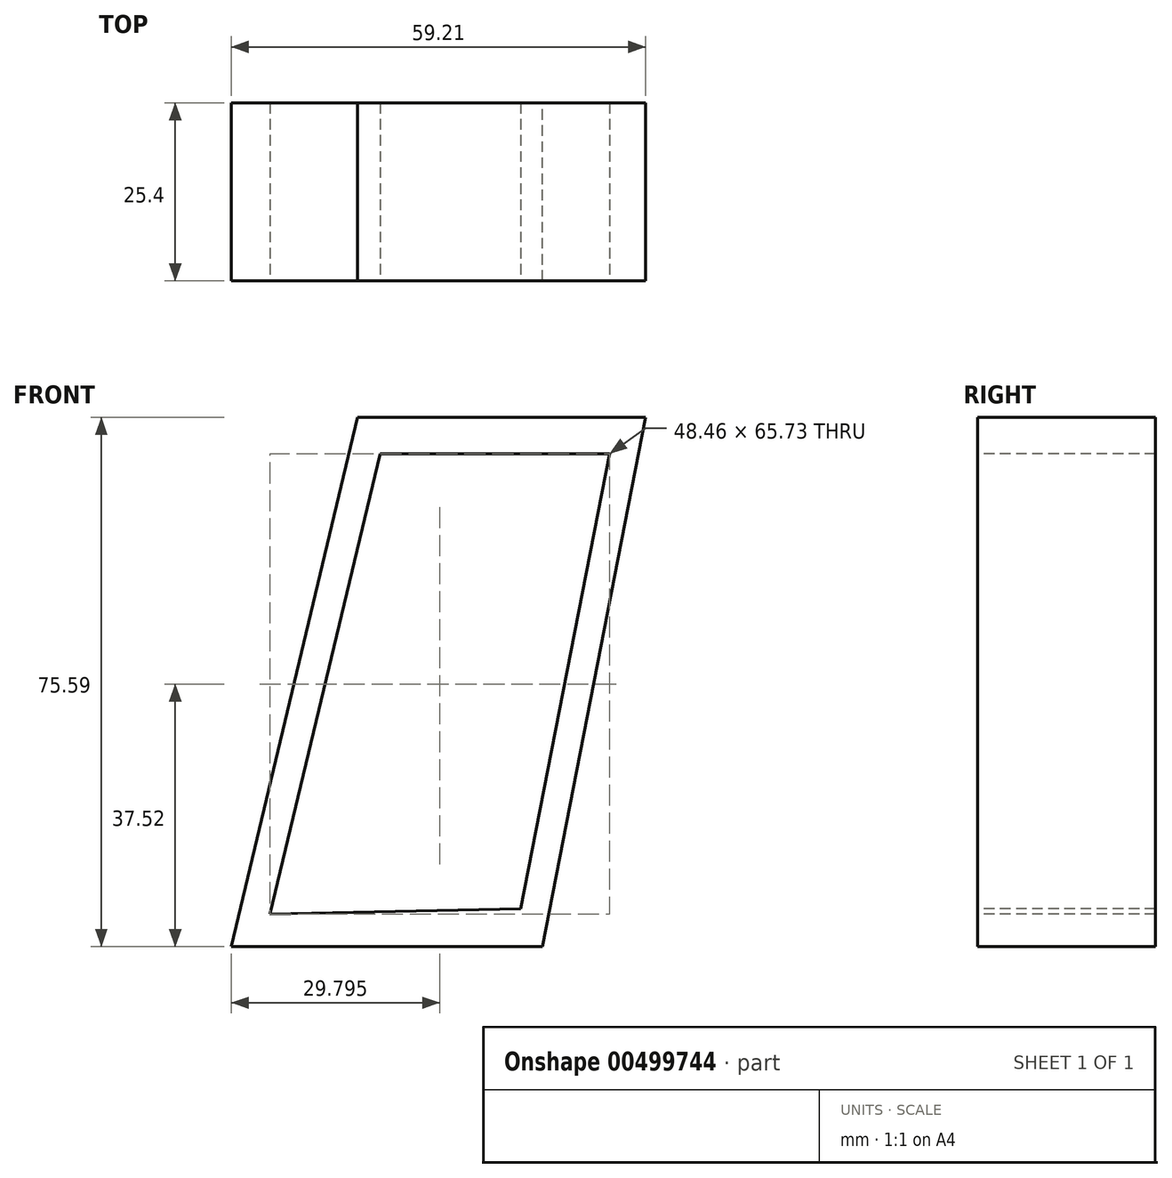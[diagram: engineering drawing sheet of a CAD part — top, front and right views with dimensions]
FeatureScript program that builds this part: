
annotation { "Feature Type Name" : "Feature", "Feature Type Description" : "" }
export const myFeature = defineFeature(function(context is Context, id is Id, definition is map)
    precondition{}
    {
        {
            var Q0;
            Q0=qCreatedBy(makeId("Front.planeOp"),FACE);
            var sketch = newSketch(context, id + "F0", { "sketchPlane" : qUnion([Q0])});
            skLineSegment(sketch, "E0", {"start": v(-26.4, 53.23) * mm, "end": v(14.76, 53.23) * mm});
            skLineSegment(sketch, "E1", {"start": v(-26.4, 53.23) * mm, "end": v(-26.4, -22.36) * mm});
            skLineSegment(sketch, "E2", {"start": v(14.76, 53.23) * mm, "end": v(-44.45, -22.36) * mm});
            skLineSegment(sketch, "E3", {"start": v(14.76, 53.23) * mm, "end": v(0, -22.36) * mm});
            skLineSegment(sketch, "E4", {"start": v(0, -22.36) * mm, "end": v(-44.45, -22.36) * mm});
            skLineSegment(sketch, "E5", {"start": v(0, -22.36) * mm, "end": v(-26.4, 53.23) * mm});
            skLineSegment(sketch, "E6", {"start": v(-44.45, -22.36) * mm, "end": v(-26.4, 53.23) * mm});
            skSolve(sketch);
        }
        {
            var Q0;
            Q0 = qSketchRegion(id + "F0", true);
            extrude(context, id + "F1", {"entities" : qUnion([Q0]), "depth" : 25.4 * mm});
        }
        {
            var Q0;
            Q0=makeQuery(id+"F1.opExtrude","CAP_FACE",FACE,{"disambiguationData":[OSD([sQuery(id+"F0.wireOp",EDGE,"E0"),sQuery(id+"F0.wireOp",EDGE,"E3"),sQuery(id+"F0.wireOp",EDGE,"E4"),sQuery(id+"F0.wireOp",EDGE,"E6")])],"isStart":false});
            var sketch = newSketch(context, id + "F2", { "sketchPlane" : qUnion([Q0])});
            skLineSegment(sketch, "E7", {"start": v(-38.88, -17.7) * mm, "end": v(-23.18, 48.02) * mm});
            skLineSegment(sketch, "E8", {"start": v(-23.18, 48.02) * mm, "end": v(9.57, 48.02) * mm});
            skLineSegment(sketch, "E9", {"start": v(9.57, 48.02) * mm, "end": v(-3.1, -16.94) * mm});
            skLineSegment(sketch, "E10", {"start": v(-3.1, -16.94) * mm, "end": v(-38.88, -17.7) * mm});
            skSolve(sketch);
        }
        {
            var Q0;
            Q0=makeQuery(id+"F2.imprint","IMPRINT",FACE,{"disambiguationData":[TD([[makeQuery(id+"F2.imprint","IMPRINT",EDGE,{"derivedFrom":sQuery(id+"F2.wireOp",EDGE,"E7")}),-1.0]])]});
            extrude(context, id + "F3", {"entities" : qUnion([Q0]), "operationType" : NewBodyOperationType.REMOVE, "oppositeDirection" : true, "depth" : 76.2 * mm});
        }
    });
